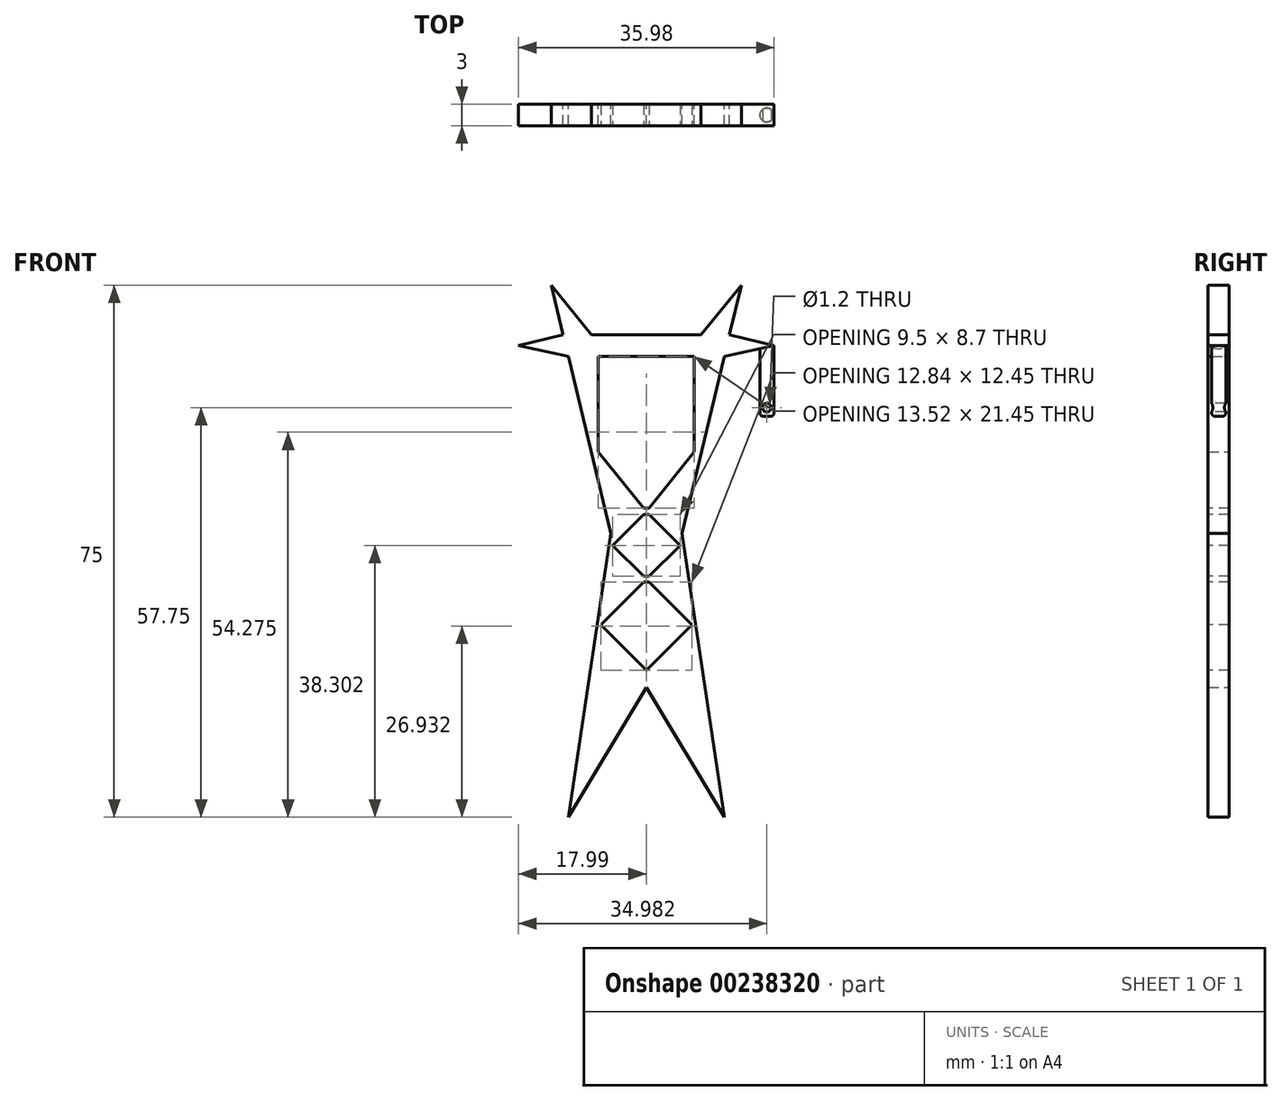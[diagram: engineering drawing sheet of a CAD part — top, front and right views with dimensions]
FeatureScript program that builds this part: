
annotation { "Feature Type Name" : "Feature", "Feature Type Description" : "" }
export const myFeature = defineFeature(function(context is Context, id is Id, definition is map)
    precondition{}
    {
        {
            var Q0;
            Q0=qCreatedBy(makeId("Front.planeOp"),FACE);
            var sketch = newSketch(context, id + "F0", { "sketchPlane" : qUnion([Q0])});
            skLineSegment(sketch, "E0", {"start": v(-11, 0) * mm, "end": v(0, 18.32) * mm});
            skLineSegment(sketch, "E1", {"start": v(-5, 40) * mm, "end": v(-11, 0) * mm});
            skLineSegment(sketch, "E2", {"start": v(-5, 40) * mm, "end": v(-11, 65) * mm});
            skLineSegment(sketch, "E3", {"start": v(-18, 66.5) * mm, "end": v(-11.71, 68) * mm});
            skLineSegment(sketch, "E4", {"start": v(-18, 66.5) * mm, "end": v(-11, 65) * mm});
            skPoint(sketch, "E5.orphan", {"position": v(-18, 65) * mm});
            skPoint(sketch, "E6.start.orphan", {"position": v(-18, 68) * mm});
            skLineSegment(sketch, "E7", {"start": v(-7.71, 68) * mm, "end": v(-13.39, 75) * mm});
            skLineSegment(sketch, "E8", {"start": v(-7.71, 68) * mm, "end": v(0, 68) * mm});
            skLineSegment(sketch, "E9", {"start": v(-6.76, 65) * mm, "end": v(0, 65) * mm});
            skLineSegment(sketch, "E10.trimOffspring", {"start": v(-11.71, 68) * mm, "end": v(-13.39, 75) * mm});
            skPoint(sketch, "E11.orphan", {"position": v(-6.76, 51.54) * mm});
            skPoint(sketch, "E12.start.orphan", {"position": v(-7.71, 51.31) * mm});
            skLineSegment(sketch, "E13", {"start": v(-6.76, 51.54) * mm, "end": v(0, 43.05) * mm});
            skLineSegment(sketch, "E14", {"start": v(-6.76, 51.54) * mm, "end": v(-6.76, 65) * mm});
            skLineSegment(sketch, "E15.MirrorCS", {"start": v(11, 0) * mm, "end": v(0, 18.32) * mm});
            skLineSegment(sketch, "E16.MirrorCS", {"start": v(5, 40) * mm, "end": v(11, 0) * mm});
            skLineSegment(sketch, "E17.MirrorCS", {"start": v(6.76, 51.54) * mm, "end": v(6.76, 65) * mm});
            skLineSegment(sketch, "E18.MirrorCS", {"start": v(6.76, 65) * mm, "end": v(0, 65) * mm});
            skPoint(sketch, "E19.MirrorP", {"position": v(18, 65) * mm});
            skLineSegment(sketch, "E20.MirrorCS", {"start": v(6.76, 51.54) * mm, "end": v(0, 43.05) * mm});
            skPoint(sketch, "E21.MirrorP", {"position": v(6.76, 51.54) * mm});
            skLineSegment(sketch, "E22.MirrorCS", {"start": v(7.71, 68) * mm, "end": v(0, 68) * mm});
            skLineSegment(sketch, "E23.MirrorCS", {"start": v(7.71, 68) * mm, "end": v(13.39, 75) * mm});
            skLineSegment(sketch, "E24.MirrorCS", {"start": v(18, 66.5) * mm, "end": v(11.71, 68) * mm});
            skPoint(sketch, "E25.MirrorP", {"position": v(7.71, 51.31) * mm});
            skLineSegment(sketch, "E26.MirrorCS", {"start": v(18, 66.5) * mm, "end": v(11, 65) * mm});
            skLineSegment(sketch, "E27.MirrorCS", {"start": v(11.71, 68) * mm, "end": v(13.39, 75) * mm});
            skPoint(sketch, "E28.MirrorP", {"position": v(18, 68) * mm});
            skLineSegment(sketch, "E29.MirrorCS", {"start": v(5, 40) * mm, "end": v(11, 65) * mm});
            skSolve(sketch);
        }
        {
            var Q0;
            Q0=makeQuery(id+"F0.imprint","IMPRINT",FACE,{"disambiguationData":[TD([[makeQuery(id+"F0.imprint","IMPRINT",EDGE,{"derivedFrom":sQuery(id+"F0.wireOp",EDGE,"E0")}),1.0]])]});
            extrude(context, id + "F1", {"entities" : qUnion([Q0]), "depth" : 3 * mm});
        }
        {
            var Q0;
            Q0=makeQuery(id+"F1.opExtrude","CAP_FACE",FACE,{"disambiguationData":[OSD([sQuery(id+"F0.wireOp",EDGE,"E0"),sQuery(id+"F0.wireOp",EDGE,"E1"),sQuery(id+"F0.wireOp",EDGE,"E2"),sQuery(id+"F0.wireOp",EDGE,"E3"),sQuery(id+"F0.wireOp",EDGE,"E4"),sQuery(id+"F0.wireOp",EDGE,"E7"),sQuery(id+"F0.wireOp",EDGE,"E8"),sQuery(id+"F0.wireOp",EDGE,"E9"),sQuery(id+"F0.wireOp",EDGE,"E10.trimOffspring"),sQuery(id+"F0.wireOp",EDGE,"E13"),sQuery(id+"F0.wireOp",EDGE,"E14"),sQuery(id+"F0.wireOp",EDGE,"E15.MirrorCS"),sQuery(id+"F0.wireOp",EDGE,"E16.MirrorCS"),sQuery(id+"F0.wireOp",EDGE,"E17.MirrorCS"),sQuery(id+"F0.wireOp",EDGE,"E18.MirrorCS"),sQuery(id+"F0.wireOp",EDGE,"E20.MirrorCS"),sQuery(id+"F0.wireOp",EDGE,"E22.MirrorCS"),sQuery(id+"F0.wireOp",EDGE,"E23.MirrorCS"),sQuery(id+"F0.wireOp",EDGE,"E24.MirrorCS"),sQuery(id+"F0.wireOp",EDGE,"E26.MirrorCS"),sQuery(id+"F0.wireOp",EDGE,"E27.MirrorCS"),sQuery(id+"F0.wireOp",EDGE,"E29.MirrorCS")])],"isStart":false});
            var sketch = newSketch(context, id + "F2", { "sketchPlane" : qUnion([Q0])});
            skLineSegment(sketch, "E30.0", {"start": v(4.5, 40.02) * mm, "end": v(10.5, 65.12) * mm});
            skLineSegment(sketch, "E30.1", {"start": v(4.5, 40.02) * mm, "end": v(10.5, -0.07) * mm});
            skLineSegment(sketch, "E31.0", {"start": v(-4.5, 40.02) * mm, "end": v(-10.5, 65.12) * mm});
            skLineSegment(sketch, "E31.1", {"start": v(-4.5, 40.02) * mm, "end": v(-10.5, -0.07) * mm});
            skLineSegment(sketch, "E32", {"start": v(0, 43.55) * mm, "end": v(0.4, 43.55) * mm});
            skLineSegment(sketch, "E33", {"start": v(0.4, 43.55) * mm, "end": v(-0.4, 43.55) * mm});
            skPoint(sketch, "E34.orphan", {"position": v(6.76, 51.54) * mm});
            skPoint(sketch, "E35.orphan", {"position": v(-6.76, 51.54) * mm});
            skPoint(sketch, "E36.endSnap0", {"position": v(0, 35.53) * mm});
            skLineSegment(sketch, "E37", {"start": v(-4.5, 40.02) * mm, "end": v(-3.03, 40.02) * mm});
            skLineSegment(sketch, "E38", {"start": v(0.4, 42.65) * mm, "end": v(4.75, 38.3) * mm});
            skLineSegment(sketch, "E39.MirrorCS", {"start": v(-0.4, 42.65) * mm, "end": v(-4.75, 38.3) * mm});
            skLineSegment(sketch, "E40.MirrorCS", {"start": v(-6.42, 27.13) * mm, "end": v(-0.4, 33.16) * mm});
            skLineSegment(sketch, "E41.MirrorCS", {"start": v(6.42, 27.13) * mm, "end": v(0.4, 33.16) * mm});
            skPoint(sketch, "E42.orphan", {"position": v(0, 33.55) * mm});
            skLineSegment(sketch, "E43.MirrorCS", {"start": v(-6.42, 27.13) * mm, "end": v(0, 20.7) * mm});
            skLineSegment(sketch, "E44.MirrorCS", {"start": v(6.42, 27.13) * mm, "end": v(0, 20.7) * mm});
            skPoint(sketch, "E45.orphan", {"position": v(4.75, 15.96) * mm});
            skPoint(sketch, "E46.orphan", {"position": v(-4.75, 15.96) * mm});
            skLineSegment(sketch, "E47.trimOffspring", {"start": v(3.03, 40.02) * mm, "end": v(4.5, 40.02) * mm});
            skLineSegment(sketch, "E48", {"start": v(0.4, 43.55) * mm, "end": v(0.4, 42.65) * mm});
            skLineSegment(sketch, "E49", {"start": v(-0.4, 43.55) * mm, "end": v(-0.4, 42.65) * mm});
            skLineSegment(sketch, "E50.trimOffspring", {"start": v(0.4, 33.95) * mm, "end": v(4.75, 38.3) * mm});
            skLineSegment(sketch, "E51.trimOffspring", {"start": v(-0.4, 33.95) * mm, "end": v(-4.75, 38.3) * mm});
            skLineSegment(sketch, "E52.trimOffspring", {"start": v(-0.4, 33.95) * mm, "end": v(-0.4, 33.16) * mm});
            skLineSegment(sketch, "E53.trimOffspring", {"start": v(0.4, 33.95) * mm, "end": v(0.4, 33.16) * mm});
            skSolve(sketch);
        }
        {
            var Q0;
            Q0=makeQuery(id+"F2.imprint","IMPRINT",FACE,{"disambiguationData":[TD([[makeQuery(id+"F2.imprint","IMPRINT",EDGE,{"derivedFrom":sQuery(id+"F2.wireOp",EDGE,"E40.MirrorCS")}),-1.0]])]});
            extrude(context, id + "F3", {"entities" : qUnion([Q0]), "operationType" : NewBodyOperationType.REMOVE, "oppositeDirection" : true, "depth" : 25 * mm});
        }
        {
            var Q0;
            Q0=makeQuery(id+"F3.boolean.opBoolean","COPY",FACE,{"derivedFrom":makeQuery(id+"F3.opExtrude","SWEPT_FACE",FACE,{"disambiguationData":[OSD([sQuery(id+"F2.wireOp",EDGE,"E52.trimOffspring")])]})});
            var sketch = newSketch(context, id + "F4", { "sketchPlane" : qUnion([Q0])});
            skLineSegment(sketch, "E54.0", {"start": v(-3, 33.95) * mm, "end": v(-3, 33.16) * mm});
            skLineSegment(sketch, "E54.1", {"start": v(0, 33.95) * mm, "end": v(-3, 33.95) * mm});
            skLineSegment(sketch, "E54.2", {"start": v(0, 33.16) * mm, "end": v(-3, 33.16) * mm});
            skLineSegment(sketch, "E54.3", {"start": v(0, 33.95) * mm, "end": v(0, 33.16) * mm});
            skLineSegment(sketch, "E55.0", {"start": v(-3, 43.55) * mm, "end": v(-3, 42.65) * mm});
            skLineSegment(sketch, "E55.1", {"start": v(0, 43.55) * mm, "end": v(-3, 43.55) * mm});
            skLineSegment(sketch, "E55.2", {"start": v(0, 43.55) * mm, "end": v(0, 42.65) * mm});
            skLineSegment(sketch, "E55.3", {"start": v(0, 42.65) * mm, "end": v(-3, 42.65) * mm});
            skSolve(sketch);
        }
        {
            var Q0;
            Q0 = qSketchRegion(id + "F4", true);
            extrude(context, id + "F5", {"entities" : qUnion([Q0]), "operationType" : NewBodyOperationType.ADD, "endBound" : BoundingType.UP_TO_NEXT, "depth" : 25 * mm});
        }
        {
            var Q0;
            Q0=makeQuery(id+"F1.opExtrude","SWEPT_EDGE",EDGE,{"disambiguationData":[OSD([sQuery(id+"F0.wireOp",EDGE,"E24.MirrorCS"),sQuery(id+"F0.wireOp",EDGE,"E26.MirrorCS")])]});
            cPoint(context, id + "F6", {"entities" : qUnion([Q0]), "parameter" : 0.5});
        }
        {
            var Q0;
            Q0=makeQuery(id+"F1.opExtrude","SWEPT_FACE",FACE,{"disambiguationData":[OSD([sQuery(id+"F0.wireOp",EDGE,"E9"),sQuery(id+"F0.wireOp",EDGE,"E18.MirrorCS")])]});
            var Q1;
            Q1 = qCreatedBy(id + "F6" ,VERTEX);
            cPlane(context, id + "F7", {"entities" : qUnion([Q0, Q1]), "cplaneType" : CPlaneType.PLANE_POINT, "offset" : 25 * mm, "width" : 150 * mm, "height" : 150 * mm});
        }
        {
            var Q0;
            Q0=qCreatedBy(id+"F7.planeOp",FACE);
            var sketch = newSketch(context, id + "F8", { "sketchPlane" : qUnion([Q0])});
            skLineSegment(sketch, "E56.0", {"start": v(18, 3) * mm, "end": v(18, 0) * mm});
            skLineSegment(sketch, "E56.1", {"start": v(18, 3) * mm, "end": v(11, 3) * mm});
            skLineSegment(sketch, "E56.2", {"start": v(18, 0) * mm, "end": v(11, 0) * mm});
            skLineSegment(sketch, "E57", {"start": v(18, 1.5) * mm, "end": v(17, 1.5) * mm});
            skCircle(sketch, "E58", {"center": v(17, 1.5) * mm, "radius": 1 * mm});
            skSolve(sketch);
        }
        {
            var Q0;
            Q0 = qSketchRegion(id + "F8", true);
            extrude(context, id + "F9", {"entities" : qUnion([Q0]), "operationType" : NewBodyOperationType.ADD, "depth" : 10 * mm});
        }
        {
            var Q0;
            Q0=makeQuery(id+"F5.boolean.opBoolean","MERGE",FACE,{"derivedFrom":[makeQuery(id+"F1.opExtrude","CAP_FACE",FACE,{"disambiguationData":[OSD([sQuery(id+"F0.wireOp",EDGE,"E0"),sQuery(id+"F0.wireOp",EDGE,"E1"),sQuery(id+"F0.wireOp",EDGE,"E2"),sQuery(id+"F0.wireOp",EDGE,"E3"),sQuery(id+"F0.wireOp",EDGE,"E4"),sQuery(id+"F0.wireOp",EDGE,"E7"),sQuery(id+"F0.wireOp",EDGE,"E8"),sQuery(id+"F0.wireOp",EDGE,"E9"),sQuery(id+"F0.wireOp",EDGE,"E10.trimOffspring"),sQuery(id+"F0.wireOp",EDGE,"E13"),sQuery(id+"F0.wireOp",EDGE,"E14"),sQuery(id+"F0.wireOp",EDGE,"E15.MirrorCS"),sQuery(id+"F0.wireOp",EDGE,"E16.MirrorCS"),sQuery(id+"F0.wireOp",EDGE,"E17.MirrorCS"),sQuery(id+"F0.wireOp",EDGE,"E18.MirrorCS"),sQuery(id+"F0.wireOp",EDGE,"E20.MirrorCS"),sQuery(id+"F0.wireOp",EDGE,"E22.MirrorCS"),sQuery(id+"F0.wireOp",EDGE,"E23.MirrorCS"),sQuery(id+"F0.wireOp",EDGE,"E24.MirrorCS"),sQuery(id+"F0.wireOp",EDGE,"E26.MirrorCS"),sQuery(id+"F0.wireOp",EDGE,"E27.MirrorCS"),sQuery(id+"F0.wireOp",EDGE,"E29.MirrorCS")])],"isStart":false}),makeQuery(id+"F5.opExtrude","SWEPT_FACE",FACE,{"disambiguationData":[OSD([sQuery(id+"F4.wireOp",EDGE,"E54.0")])]}),makeQuery(id+"F5.opExtrude","SWEPT_FACE",FACE,{"disambiguationData":[OSD([sQuery(id+"F4.wireOp",EDGE,"E55.0")])]})]});
            var sketch = newSketch(context, id + "F10", { "sketchPlane" : qUnion([Q0])});
            skLineSegment(sketch, "E59.0", {"start": v(18, 56.5) * mm, "end": v(16, 56.5) * mm});
            skLineSegment(sketch, "E60", {"start": v(17, 56.5) * mm, "end": v(17, 57.75) * mm});
            skCircle(sketch, "E61", {"center": v(17, 57.75) * mm, "radius": 0.6 * mm});
            skSolve(sketch);
        }
        {
            var Q0;
            Q0 = qSketchRegion(id + "F10", true);
            extrude(context, id + "F11", {"entities" : qUnion([Q0]), "operationType" : NewBodyOperationType.REMOVE, "oppositeDirection" : true, "depth" : 25 * mm});
        }
        {
            var Q0;
            Q0=makeQuery(id+"F9.opExtrude","CAP_EDGE",EDGE,{"disambiguationData":[OSD([sQuery(id+"F8.wireOp",EDGE,"E58")])],"isStart":false});
            fillet(context, id + "F12", {"entities" : qUnion([Q0]), "radius" : 0.5 * mm, "tangentPropagation" : true, "allowEdgeOverflow" : false});
        }
    });
